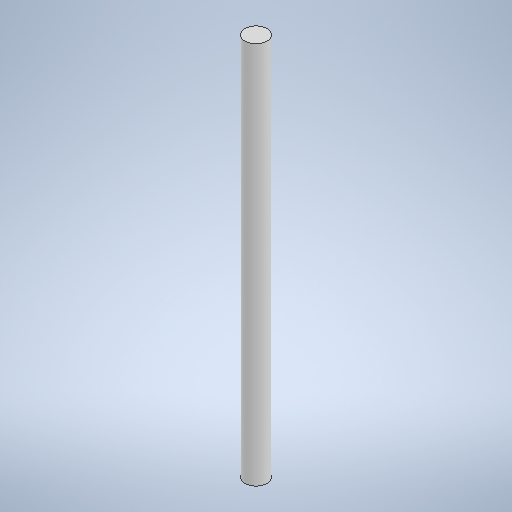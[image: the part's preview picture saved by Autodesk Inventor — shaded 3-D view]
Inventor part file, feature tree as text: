
AUTODESK INVENTOR PART (.ipt)
format: ipt  version: 2025.1 (Build 291241000, 241)  size: 248,320 bytes
history: native  units: mm
features: extrude x1, sketch x1
ambient origin geometry x8: Origin, YZ Plane, XZ Plane, XY Plane, X Axis, Y Axis, Z Axis, Center Point
bodies: Solid1 (feature_tree)
feature tree (2):
  extrude  "Extrusion1"  Depth=87.5mm TaperAngle=0.0deg
  sketch  "Sketch1"  dims[d0=5.0mm d1=87.5mm d2=0.0mm]
